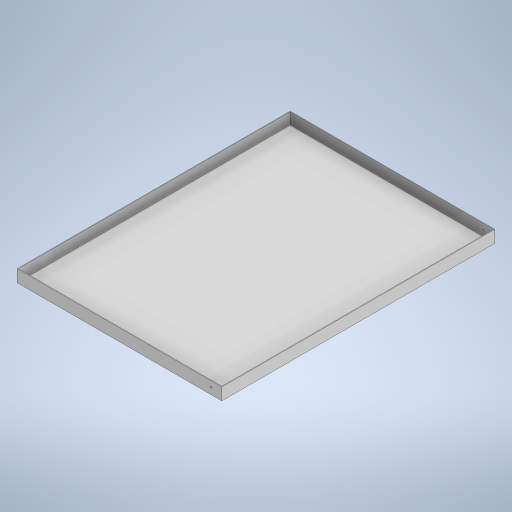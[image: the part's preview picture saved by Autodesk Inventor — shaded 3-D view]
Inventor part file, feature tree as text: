
AUTODESK INVENTOR PART (.ipt)
format: ipt  version: 2024 (Build 280153000, 153)  size: 251,392 bytes
history: native  units: mm
features: extrude x3, sketch x3, other x1
ambient origin geometry x8: Origin, YZ Plane, XZ Plane, XY Plane, X Axis, Y Axis, Z Axis, Center Point
bodies: Body1 (feature_tree)
feature tree (7):
  other  "Sólido1"
  extrude  "Extrusión1"  Depth=1200.0mm
  extrude  "Extrusión2"  Depth=3.0mm
  extrude  "Extrusión3"  Depth=50.0mm
  sketch  "Boceto1"  dims[d0=900.0mm d1=1200.0mm]
  sketch  "Boceto2"  dims[d2=3.0mm d3=0.0mm d4=3.0mm]
  sketch  "Boceto3"  dims[d5=50.0mm d6=0.0mm d7=8.0mm d8=25.0mm d9=3.0mm d10=50.0mm d11=1243.5mm d12=0.0mm]
